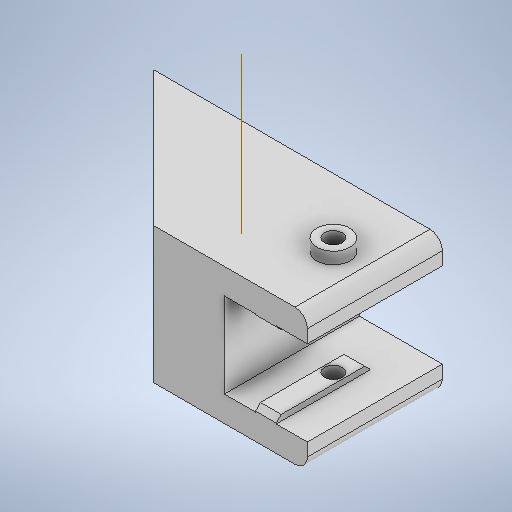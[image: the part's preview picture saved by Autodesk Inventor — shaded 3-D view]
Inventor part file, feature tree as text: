
AUTODESK INVENTOR PART (.ipt)
format: ipt  version: 2025 (Build 290162010, 162A)  size: 379,904 bytes
history: native  units: in
note: dims shown in document units (in); Inventor stores cm internally (conversion verified against a paired STEP export)
features: extrude x10, sketch x10, chamfer x2, plane x1, other x1, fillet x1
ambient origin geometry x8: Origin, YZ Plane, XZ Plane, XY Plane, X Axis, Y Axis, Z Axis, Center Point
bodies: Volumenkörper1 (feature_tree)
feature tree (25):
  extrude  "Extrusion1"  TaperAngle=45.0deg  [1 undecoded]
  extrude  "Extrusion2"  Depth=1.2913in
  extrude  "Extrusion6"  Depth=1.2913in
  plane  "Arbeitsebene1"
  other  "Verdickung1"
  extrude  "Extrusion7"  Depth=0.7087in
  extrude  "Extrusion8"  [1 undecoded]
  chamfer  "Fasen2"  Distance=1.4567in
  extrude  "Extrusion10"  Depth=0.3445in
  extrude  "Extrusion11"  Depth=0.1969in TaperAngle=0.0deg
  chamfer  "Fasen3"  Distance=0.0394in Angle=45.0deg
  fillet  "Rundung1"  Radius=0.1969in
  extrude  "Extrusion13"  Depth=0.3937in TaperAngle=0.0deg
  extrude  "Extrusion14"  Depth=0.3937in
  extrude  "Extrusion15"  Depth=0.3937in TaperAngle=45.0deg
  sketch  "Skizze1"  dims[d0=1.811in d1=45.0deg]
  sketch  "Skizze2"  dims[d2=1.2913in d3=0.0in d5=0.1673in]
  sketch  "Skizze6"  dims[d7=1.2913in d8=0.5709in]
  sketch  "Skizze7"  dims[d9=0.6693in d10=0.7087in]
  sketch  "Skizze8"  dims[d11=0.0in d12=0.0in d19=-0.5906in]
  sketch  "Skizze10"  dims[d34=0.8071in d35=1.4567in d36=0.0in]
  sketch  "Skizze11"  dims[d37=0.6693in d38=0.0394in d39=0.3445in]
  sketch  "Skizze13"  dims[d40=0.1378in d41=0.7874in d42=0.0in d43=0.0in d44=0.1378in d45=0.1969in d46=0.0in d47=0.0in d48=0.0394in d49=0.0787in d50=45.0deg d56=0.1969in]
  sketch  "Skizze14"  dims[d57=0.3937in d58=0.0551in d59=0.0in]
  sketch  "Skizze15"  dims[d60=0.0551in d61=0.0in d64=0.2953in d67=0.0472in d68=0.0787in d69=45.0deg d70=0.1181in d71=0.315in d72=0.1122in d73=0.0in d74=0.1122in d75=0.0in d78=0.1673in d79=0.3937in d80=0.0in d81=0.0in]
note: 2 required parameter values undecoded (feature->parameter linkage not recoverable at this tier; creation-order binding heuristic only, values carry confidence <= 0.55)
